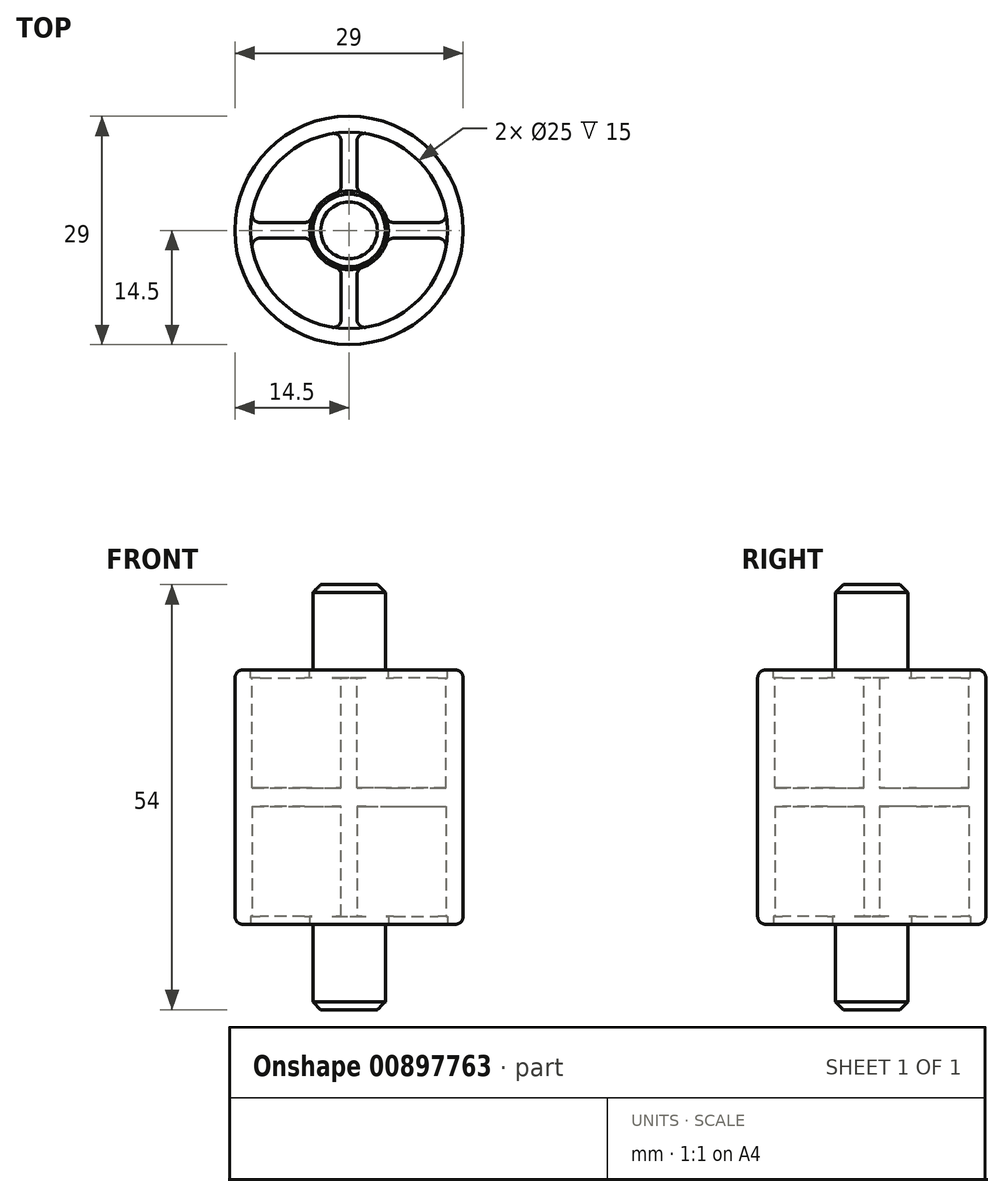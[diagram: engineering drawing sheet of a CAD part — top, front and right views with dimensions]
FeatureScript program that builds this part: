
annotation { "Feature Type Name" : "Feature", "Feature Type Description" : "" }
export const myFeature = defineFeature(function(context is Context, id is Id, definition is map)
    precondition{}
    {
        {
            var Q0;
            Q0=qCreatedBy(makeId("Front.planeOp"),FACE);
            var sketch = newSketch(context, id + "F0", { "sketchPlane" : qUnion([Q0])});
            skLineSegment(sketch, "E0", {"start": v(0, 27) * mm, "end": v(0, -27) * mm});
            skLineSegment(sketch, "E1", {"start": v(0, -27) * mm, "end": v(4.6, -27) * mm});
            skLineSegment(sketch, "E2", {"start": v(4.6, -27) * mm, "end": v(4.6, -16.15) * mm});
            skLineSegment(sketch, "E3", {"start": v(4.6, -16.15) * mm, "end": v(14.5, -16.15) * mm});
            skLineSegment(sketch, "E4", {"start": v(14.5, -16.15) * mm, "end": v(14.5, 16.15) * mm});
            skLineSegment(sketch, "E5", {"start": v(14.5, 16.15) * mm, "end": v(4.6, 16.15) * mm});
            skLineSegment(sketch, "E6", {"start": v(4.6, 16.15) * mm, "end": v(4.6, 27) * mm});
            skLineSegment(sketch, "E7", {"start": v(4.6, 27) * mm, "end": v(0, 27) * mm});
            skSolve(sketch);
        }
        {
            var Q0;
            Q0=makeQuery(id+"F0.imprint","IMPRINT",FACE,{"disambiguationData":[TD([[makeQuery(id+"F0.imprint","IMPRINT",EDGE,{"derivedFrom":sQuery(id+"F0.wireOp",EDGE,"E0")}),1.0]])]});
            var Q1;
            Q1=sQuery(id+"F0.wireOp",EDGE,"E0");
            revolve(context, id + "F1", {"surfaceOperationType" : NewSurfaceOperationType.NEW, "entities" : qUnion([Q0]), "axis" : qUnion([Q1]), "revolveType" : RevolveType.FULL});
        }
        {
            var Q0;
            Q0=makeQuery(id+"F1.opRevolve","SWEPT_FACE",FACE,{"disambiguationData":[OSD([sQuery(id+"F0.wireOp",EDGE,"E5")])]});
            var sketch = newSketch(context, id + "F2", { "sketchPlane" : qUnion([Q0])});
            skArc(sketch, "E8", {"start": v(12.46, 1) * mm, "mid": v(8.84, 8.84) * mm, "end": v(1, 12.46) * mm});
            skArc(sketch, "E9", {"start": v(4.9, 1) * mm, "mid": v(3.54, 3.54) * mm, "end": v(1, 4.9) * mm});
            skLineSegment(sketch, "E10", {"start": v(1, 4.9) * mm, "end": v(1, 12.46) * mm});
            skLineSegment(sketch, "E11", {"start": v(4.9, 1) * mm, "end": v(12.46, 1) * mm});
            skSolve(sketch);
        }
        {
            var Q0;
            Q0=makeQuery(id+"F2.imprint","IMPRINT",FACE,{"disambiguationData":[TD([[makeQuery(id+"F2.imprint","IMPRINT",EDGE,{"derivedFrom":sQuery(id+"F2.wireOp",EDGE,"E8")}),1.0]])]});
            extrude(context, id + "F3", {"entities" : qUnion([Q0]), "oppositeDirection" : true, "depth" : 15 * mm, "offsetDistance" : 25 * mm});
        }
        {
            var Q0;
            Q0=makeQuery(id+"F3.opExtrude","SWEPT_BODY",BODY,{"disambiguationData":[OSD([sQuery(id+"F2.wireOp",EDGE,"E8"),sQuery(id+"F2.wireOp",EDGE,"E9"),sQuery(id+"F2.wireOp",EDGE,"E10"),sQuery(id+"F2.wireOp",EDGE,"E11")])]});
            var Q1;
            Q1=makeQuery(id+"F1.opRevolve","SWEPT_FACE",FACE,{"disambiguationData":[OSD([sQuery(id+"F0.wireOp",EDGE,"E6")])]});
            circularPattern(context, id + "F4", {"entities" : qUnion([Q0]), "axis" : qUnion([Q1]), "angle" : 360 * degree, "instanceCount" : 4, "equalSpace" : true});
        }
        {
            var Q0;
            Q0=makeQuery(id+"F3.opExtrude","SWEPT_BODY",BODY,{"disambiguationData":[OSD([sQuery(id+"F2.wireOp",EDGE,"E8"),sQuery(id+"F2.wireOp",EDGE,"E9"),sQuery(id+"F2.wireOp",EDGE,"E10"),sQuery(id+"F2.wireOp",EDGE,"E11")])]});
            var Q1;
            Q1=makeQuery(id+"F4.opPattern","COPY",BODY,{"derivedFrom":makeQuery(id+"F3.opExtrude","SWEPT_BODY",BODY,{"disambiguationData":[OSD([sQuery(id+"F2.wireOp",EDGE,"E8"),sQuery(id+"F2.wireOp",EDGE,"E9"),sQuery(id+"F2.wireOp",EDGE,"E10"),sQuery(id+"F2.wireOp",EDGE,"E11")])]}),"instanceName":"1"});
            var Q2;
            Q2=makeQuery(id+"F4.opPattern","COPY",BODY,{"derivedFrom":makeQuery(id+"F3.opExtrude","SWEPT_BODY",BODY,{"disambiguationData":[OSD([sQuery(id+"F2.wireOp",EDGE,"E8"),sQuery(id+"F2.wireOp",EDGE,"E9"),sQuery(id+"F2.wireOp",EDGE,"E10"),sQuery(id+"F2.wireOp",EDGE,"E11")])]}),"instanceName":"2"});
            var Q3;
            Q3=makeQuery(id+"F4.opPattern","COPY",BODY,{"derivedFrom":makeQuery(id+"F3.opExtrude","SWEPT_BODY",BODY,{"disambiguationData":[OSD([sQuery(id+"F2.wireOp",EDGE,"E8"),sQuery(id+"F2.wireOp",EDGE,"E9"),sQuery(id+"F2.wireOp",EDGE,"E10"),sQuery(id+"F2.wireOp",EDGE,"E11")])]}),"instanceName":"3"});
            var Q4;
            Q4=qCreatedBy(makeId("Top.planeOp"),FACE);
            mirror(context, id + "F5", {"entities" : qUnion([Q0, Q1, Q2, Q3]), "mirrorPlane" : qUnion([Q4])});
        }
        {
            var Q0;
            Q0=makeQuery(id+"F3.opExtrude","SWEPT_BODY",BODY,{"disambiguationData":[OSD([sQuery(id+"F2.wireOp",EDGE,"E8"),sQuery(id+"F2.wireOp",EDGE,"E9"),sQuery(id+"F2.wireOp",EDGE,"E10"),sQuery(id+"F2.wireOp",EDGE,"E11")])]});
            var Q1;
            Q1=makeQuery(id+"F4.opPattern","COPY",BODY,{"derivedFrom":makeQuery(id+"F3.opExtrude","SWEPT_BODY",BODY,{"disambiguationData":[OSD([sQuery(id+"F2.wireOp",EDGE,"E8"),sQuery(id+"F2.wireOp",EDGE,"E9"),sQuery(id+"F2.wireOp",EDGE,"E10"),sQuery(id+"F2.wireOp",EDGE,"E11")])]}),"instanceName":"1"});
            var Q2;
            Q2=makeQuery(id+"F4.opPattern","COPY",BODY,{"derivedFrom":makeQuery(id+"F3.opExtrude","SWEPT_BODY",BODY,{"disambiguationData":[OSD([sQuery(id+"F2.wireOp",EDGE,"E8"),sQuery(id+"F2.wireOp",EDGE,"E9"),sQuery(id+"F2.wireOp",EDGE,"E10"),sQuery(id+"F2.wireOp",EDGE,"E11")])]}),"instanceName":"2"});
            var Q3;
            Q3=makeQuery(id+"F4.opPattern","COPY",BODY,{"derivedFrom":makeQuery(id+"F3.opExtrude","SWEPT_BODY",BODY,{"disambiguationData":[OSD([sQuery(id+"F2.wireOp",EDGE,"E8"),sQuery(id+"F2.wireOp",EDGE,"E9"),sQuery(id+"F2.wireOp",EDGE,"E10"),sQuery(id+"F2.wireOp",EDGE,"E11")])]}),"instanceName":"3"});
            var Q4;
            Q4=makeQuery(id+"F5.opPattern","COPY",BODY,{"derivedFrom":makeQuery(id+"F3.opExtrude","SWEPT_BODY",BODY,{"disambiguationData":[OSD([sQuery(id+"F2.wireOp",EDGE,"E8"),sQuery(id+"F2.wireOp",EDGE,"E9"),sQuery(id+"F2.wireOp",EDGE,"E10"),sQuery(id+"F2.wireOp",EDGE,"E11")])]}),"instanceName":"1"});
            var Q5;
            Q5=makeQuery(id+"F5.opPattern","COPY",BODY,{"derivedFrom":makeQuery(id+"F4.opPattern","COPY",BODY,{"derivedFrom":makeQuery(id+"F3.opExtrude","SWEPT_BODY",BODY,{"disambiguationData":[OSD([sQuery(id+"F2.wireOp",EDGE,"E8"),sQuery(id+"F2.wireOp",EDGE,"E9"),sQuery(id+"F2.wireOp",EDGE,"E10"),sQuery(id+"F2.wireOp",EDGE,"E11")])]}),"instanceName":"1"}),"instanceName":"1"});
            var Q6;
            Q6=makeQuery(id+"F5.opPattern","COPY",BODY,{"derivedFrom":makeQuery(id+"F4.opPattern","COPY",BODY,{"derivedFrom":makeQuery(id+"F3.opExtrude","SWEPT_BODY",BODY,{"disambiguationData":[OSD([sQuery(id+"F2.wireOp",EDGE,"E8"),sQuery(id+"F2.wireOp",EDGE,"E9"),sQuery(id+"F2.wireOp",EDGE,"E10"),sQuery(id+"F2.wireOp",EDGE,"E11")])]}),"instanceName":"2"}),"instanceName":"1"});
            var Q7;
            Q7=makeQuery(id+"F5.opPattern","COPY",BODY,{"derivedFrom":makeQuery(id+"F4.opPattern","COPY",BODY,{"derivedFrom":makeQuery(id+"F3.opExtrude","SWEPT_BODY",BODY,{"disambiguationData":[OSD([sQuery(id+"F2.wireOp",EDGE,"E8"),sQuery(id+"F2.wireOp",EDGE,"E9"),sQuery(id+"F2.wireOp",EDGE,"E10"),sQuery(id+"F2.wireOp",EDGE,"E11")])]}),"instanceName":"3"}),"instanceName":"1"});
            var Q8;
            Q8=makeQuery(id+"F1.opRevolve","SWEPT_BODY",BODY,{"disambiguationData":[OSD([sQuery(id+"F0.wireOp",EDGE,"E0"),sQuery(id+"F0.wireOp",EDGE,"E1"),sQuery(id+"F0.wireOp",EDGE,"E2"),sQuery(id+"F0.wireOp",EDGE,"E3"),sQuery(id+"F0.wireOp",EDGE,"E4"),sQuery(id+"F0.wireOp",EDGE,"E5"),sQuery(id+"F0.wireOp",EDGE,"E6"),sQuery(id+"F0.wireOp",EDGE,"E7")])]});
            booleanBodies(context, id + "F6", {"operationType" : BooleanOperationType.SUBTRACTION, "tools" : qUnion([Q0, Q1, Q2, Q3, Q4, Q5, Q6, Q7]), "targets" : qUnion([Q8])});
        }
        {
            var Q0;
            Q0=makeQuery(id+"F1.opRevolve","SWEPT_FACE",FACE,{"disambiguationData":[OSD([sQuery(id+"F0.wireOp",EDGE,"E5")])]});
            var sketch = newSketch(context, id + "F7", { "sketchPlane" : qUnion([Q0])});
            skCircle(sketch, "E12", {"center": v(0, 0) * mm, "radius": 12.5 * mm});
            skCircle(sketch, "E13", {"center": v(0, 0) * mm, "radius": 5 * mm});
            skSolve(sketch);
        }
        {
            var Q0;
            Q0 = qSketchRegion(id + "F7", true);
            extrude(context, id + "F8", {"entities" : qUnion([Q0]), "oppositeDirection" : true, "depth" : 1 * mm, "offsetDistance" : 25 * mm});
        }
        {
            var Q0;
            Q0=makeQuery(id+"F8.opExtrude","SWEPT_BODY",BODY,{"disambiguationData":[OSD([sQuery(id+"F7.wireOp",EDGE,"E12"),sQuery(id+"F7.wireOp",EDGE,"E13")])]});
            var Q1;
            Q1=qCreatedBy(makeId("Top.planeOp"),FACE);
            mirror(context, id + "F9", {"entities" : qUnion([Q0]), "mirrorPlane" : qUnion([Q1])});
        }
        {
            var Q0;
            Q0=makeQuery(id+"F8.opExtrude","SWEPT_BODY",BODY,{"disambiguationData":[OSD([sQuery(id+"F7.wireOp",EDGE,"E12"),sQuery(id+"F7.wireOp",EDGE,"E13")])]});
            var Q1;
            Q1=makeQuery(id+"F9.opPattern","COPY",BODY,{"derivedFrom":makeQuery(id+"F8.opExtrude","SWEPT_BODY",BODY,{"disambiguationData":[OSD([sQuery(id+"F7.wireOp",EDGE,"E12"),sQuery(id+"F7.wireOp",EDGE,"E13")])]}),"instanceName":"1"});
            var Q2;
            Q2=makeQuery(id+"F1.opRevolve","SWEPT_BODY",BODY,{"disambiguationData":[OSD([sQuery(id+"F0.wireOp",EDGE,"E0"),sQuery(id+"F0.wireOp",EDGE,"E1"),sQuery(id+"F0.wireOp",EDGE,"E2"),sQuery(id+"F0.wireOp",EDGE,"E3"),sQuery(id+"F0.wireOp",EDGE,"E4"),sQuery(id+"F0.wireOp",EDGE,"E5"),sQuery(id+"F0.wireOp",EDGE,"E6"),sQuery(id+"F0.wireOp",EDGE,"E7")])]});
            booleanBodies(context, id + "F10", {"operationType" : BooleanOperationType.SUBTRACTION, "tools" : qUnion([Q0, Q1]), "targets" : qUnion([Q2])});
        }
        {
            var Q0;
            Q0=makeQuery(id+"F1.opRevolve","SWEPT_EDGE",EDGE,{"disambiguationData":[OSD([sQuery(id+"F0.wireOp",EDGE,"E4"),sQuery(id+"F0.wireOp",EDGE,"E5")])]});
            var Q1;
            Q1=makeQuery(id+"F1.opRevolve","SWEPT_EDGE",EDGE,{"disambiguationData":[OSD([sQuery(id+"F0.wireOp",EDGE,"E3"),sQuery(id+"F0.wireOp",EDGE,"E4")])]});
            fillet(context, id + "F11", {"entities" : qUnion([Q0, Q1]), "radius" : 1 * mm, "tangentPropagation" : true, "allowEdgeOverflow" : false});
        }
        {
            var Q0;
            Q0=makeQuery(id+"F6.opBoolean","COPY",EDGE,{"derivedFrom":makeQuery(id+"F5.opPattern","COPY",EDGE,{"derivedFrom":makeQuery(id+"F4.opPattern","COPY",EDGE,{"derivedFrom":makeQuery(id+"F3.opExtrude","SWEPT_EDGE",EDGE,{"disambiguationData":[OSD([sQuery(id+"F2.wireOp",EDGE,"E8"),sQuery(id+"F2.wireOp",EDGE,"E10")])]}),"instanceName":"2"}),"instanceName":"1"})});
            var Q1;
            Q1=makeQuery(id+"F6.opBoolean","COPY",EDGE,{"derivedFrom":makeQuery(id+"F5.opPattern","COPY",EDGE,{"derivedFrom":makeQuery(id+"F4.opPattern","COPY",EDGE,{"derivedFrom":makeQuery(id+"F3.opExtrude","SWEPT_EDGE",EDGE,{"disambiguationData":[OSD([sQuery(id+"F2.wireOp",EDGE,"E8"),sQuery(id+"F2.wireOp",EDGE,"E11")])]}),"instanceName":"3"}),"instanceName":"1"})});
            var Q2;
            Q2=makeQuery(id+"F6.opBoolean","COPY",EDGE,{"derivedFrom":makeQuery(id+"F5.opPattern","COPY",EDGE,{"derivedFrom":makeQuery(id+"F4.opPattern","COPY",EDGE,{"derivedFrom":makeQuery(id+"F3.opExtrude","SWEPT_EDGE",EDGE,{"disambiguationData":[OSD([sQuery(id+"F2.wireOp",EDGE,"E9"),sQuery(id+"F2.wireOp",EDGE,"E11")])]}),"instanceName":"3"}),"instanceName":"1"})});
            var Q3;
            Q3=makeQuery(id+"F6.opBoolean","COPY",EDGE,{"derivedFrom":makeQuery(id+"F5.opPattern","COPY",EDGE,{"derivedFrom":makeQuery(id+"F4.opPattern","COPY",EDGE,{"derivedFrom":makeQuery(id+"F3.opExtrude","SWEPT_EDGE",EDGE,{"disambiguationData":[OSD([sQuery(id+"F2.wireOp",EDGE,"E9"),sQuery(id+"F2.wireOp",EDGE,"E10")])]}),"instanceName":"3"}),"instanceName":"1"})});
            var Q4;
            Q4=makeQuery(id+"F6.opBoolean","COPY",EDGE,{"derivedFrom":makeQuery(id+"F5.opPattern","COPY",EDGE,{"derivedFrom":makeQuery(id+"F4.opPattern","COPY",EDGE,{"derivedFrom":makeQuery(id+"F3.opExtrude","SWEPT_EDGE",EDGE,{"disambiguationData":[OSD([sQuery(id+"F2.wireOp",EDGE,"E8"),sQuery(id+"F2.wireOp",EDGE,"E10")])]}),"instanceName":"3"}),"instanceName":"1"})});
            var Q5;
            Q5=makeQuery(id+"F6.opBoolean","COPY",EDGE,{"derivedFrom":makeQuery(id+"F5.opPattern","COPY",EDGE,{"derivedFrom":makeQuery(id+"F3.opExtrude","SWEPT_EDGE",EDGE,{"disambiguationData":[OSD([sQuery(id+"F2.wireOp",EDGE,"E9"),sQuery(id+"F2.wireOp",EDGE,"E11")])]}),"instanceName":"1"})});
            var Q6;
            Q6=makeQuery(id+"F6.opBoolean","COPY",EDGE,{"derivedFrom":makeQuery(id+"F5.opPattern","COPY",EDGE,{"derivedFrom":makeQuery(id+"F3.opExtrude","SWEPT_EDGE",EDGE,{"disambiguationData":[OSD([sQuery(id+"F2.wireOp",EDGE,"E8"),sQuery(id+"F2.wireOp",EDGE,"E11")])]}),"instanceName":"1"})});
            var Q7;
            Q7=makeQuery(id+"F6.opBoolean","COPY",EDGE,{"derivedFrom":makeQuery(id+"F5.opPattern","COPY",EDGE,{"derivedFrom":makeQuery(id+"F3.opExtrude","SWEPT_EDGE",EDGE,{"disambiguationData":[OSD([sQuery(id+"F2.wireOp",EDGE,"E9"),sQuery(id+"F2.wireOp",EDGE,"E10")])]}),"instanceName":"1"})});
            var Q8;
            Q8=makeQuery(id+"F6.opBoolean","COPY",EDGE,{"derivedFrom":makeQuery(id+"F5.opPattern","COPY",EDGE,{"derivedFrom":makeQuery(id+"F3.opExtrude","SWEPT_EDGE",EDGE,{"disambiguationData":[OSD([sQuery(id+"F2.wireOp",EDGE,"E8"),sQuery(id+"F2.wireOp",EDGE,"E10")])]}),"instanceName":"1"})});
            var Q9;
            Q9=makeQuery(id+"F6.opBoolean","COPY",EDGE,{"derivedFrom":makeQuery(id+"F5.opPattern","COPY",EDGE,{"derivedFrom":makeQuery(id+"F4.opPattern","COPY",EDGE,{"derivedFrom":makeQuery(id+"F3.opExtrude","SWEPT_EDGE",EDGE,{"disambiguationData":[OSD([sQuery(id+"F2.wireOp",EDGE,"E9"),sQuery(id+"F2.wireOp",EDGE,"E11")])]}),"instanceName":"1"}),"instanceName":"1"})});
            var Q10;
            Q10=makeQuery(id+"F6.opBoolean","COPY",EDGE,{"derivedFrom":makeQuery(id+"F5.opPattern","COPY",EDGE,{"derivedFrom":makeQuery(id+"F4.opPattern","COPY",EDGE,{"derivedFrom":makeQuery(id+"F3.opExtrude","SWEPT_EDGE",EDGE,{"disambiguationData":[OSD([sQuery(id+"F2.wireOp",EDGE,"E8"),sQuery(id+"F2.wireOp",EDGE,"E11")])]}),"instanceName":"1"}),"instanceName":"1"})});
            var Q11;
            Q11=makeQuery(id+"F6.opBoolean","COPY",EDGE,{"derivedFrom":makeQuery(id+"F5.opPattern","COPY",EDGE,{"derivedFrom":makeQuery(id+"F4.opPattern","COPY",EDGE,{"derivedFrom":makeQuery(id+"F3.opExtrude","SWEPT_EDGE",EDGE,{"disambiguationData":[OSD([sQuery(id+"F2.wireOp",EDGE,"E9"),sQuery(id+"F2.wireOp",EDGE,"E10")])]}),"instanceName":"1"}),"instanceName":"1"})});
            var Q12;
            Q12=makeQuery(id+"F6.opBoolean","COPY",EDGE,{"derivedFrom":makeQuery(id+"F5.opPattern","COPY",EDGE,{"derivedFrom":makeQuery(id+"F4.opPattern","COPY",EDGE,{"derivedFrom":makeQuery(id+"F3.opExtrude","SWEPT_EDGE",EDGE,{"disambiguationData":[OSD([sQuery(id+"F2.wireOp",EDGE,"E8"),sQuery(id+"F2.wireOp",EDGE,"E10")])]}),"instanceName":"1"}),"instanceName":"1"})});
            var Q13;
            Q13=makeQuery(id+"F6.opBoolean","COPY",EDGE,{"derivedFrom":makeQuery(id+"F5.opPattern","COPY",EDGE,{"derivedFrom":makeQuery(id+"F4.opPattern","COPY",EDGE,{"derivedFrom":makeQuery(id+"F3.opExtrude","SWEPT_EDGE",EDGE,{"disambiguationData":[OSD([sQuery(id+"F2.wireOp",EDGE,"E9"),sQuery(id+"F2.wireOp",EDGE,"E10")])]}),"instanceName":"2"}),"instanceName":"1"})});
            var Q14;
            Q14=makeQuery(id+"F6.opBoolean","COPY",EDGE,{"derivedFrom":makeQuery(id+"F5.opPattern","COPY",EDGE,{"derivedFrom":makeQuery(id+"F4.opPattern","COPY",EDGE,{"derivedFrom":makeQuery(id+"F3.opExtrude","SWEPT_EDGE",EDGE,{"disambiguationData":[OSD([sQuery(id+"F2.wireOp",EDGE,"E9"),sQuery(id+"F2.wireOp",EDGE,"E11")])]}),"instanceName":"2"}),"instanceName":"1"})});
            var Q15;
            Q15=makeQuery(id+"F6.opBoolean","COPY",EDGE,{"derivedFrom":makeQuery(id+"F5.opPattern","COPY",EDGE,{"derivedFrom":makeQuery(id+"F4.opPattern","COPY",EDGE,{"derivedFrom":makeQuery(id+"F3.opExtrude","SWEPT_EDGE",EDGE,{"disambiguationData":[OSD([sQuery(id+"F2.wireOp",EDGE,"E8"),sQuery(id+"F2.wireOp",EDGE,"E11")])]}),"instanceName":"2"}),"instanceName":"1"})});
            var Q16;
            Q16=makeQuery(id+"F6.opBoolean","COPY",EDGE,{"derivedFrom":makeQuery(id+"F4.opPattern","COPY",EDGE,{"derivedFrom":makeQuery(id+"F3.opExtrude","SWEPT_EDGE",EDGE,{"disambiguationData":[OSD([sQuery(id+"F2.wireOp",EDGE,"E9"),sQuery(id+"F2.wireOp",EDGE,"E10")])]}),"instanceName":"2"})});
            var Q17;
            Q17=makeQuery(id+"F6.opBoolean","COPY",EDGE,{"derivedFrom":makeQuery(id+"F4.opPattern","COPY",EDGE,{"derivedFrom":makeQuery(id+"F3.opExtrude","SWEPT_EDGE",EDGE,{"disambiguationData":[OSD([sQuery(id+"F2.wireOp",EDGE,"E8"),sQuery(id+"F2.wireOp",EDGE,"E10")])]}),"instanceName":"2"})});
            var Q18;
            Q18=makeQuery(id+"F6.opBoolean","COPY",EDGE,{"derivedFrom":makeQuery(id+"F4.opPattern","COPY",EDGE,{"derivedFrom":makeQuery(id+"F3.opExtrude","SWEPT_EDGE",EDGE,{"disambiguationData":[OSD([sQuery(id+"F2.wireOp",EDGE,"E9"),sQuery(id+"F2.wireOp",EDGE,"E11")])]}),"instanceName":"3"})});
            var Q19;
            Q19=makeQuery(id+"F6.opBoolean","COPY",EDGE,{"derivedFrom":makeQuery(id+"F4.opPattern","COPY",EDGE,{"derivedFrom":makeQuery(id+"F3.opExtrude","SWEPT_EDGE",EDGE,{"disambiguationData":[OSD([sQuery(id+"F2.wireOp",EDGE,"E8"),sQuery(id+"F2.wireOp",EDGE,"E11")])]}),"instanceName":"3"})});
            var Q20;
            Q20=makeQuery(id+"F6.opBoolean","COPY",EDGE,{"derivedFrom":makeQuery(id+"F4.opPattern","COPY",EDGE,{"derivedFrom":makeQuery(id+"F3.opExtrude","SWEPT_EDGE",EDGE,{"disambiguationData":[OSD([sQuery(id+"F2.wireOp",EDGE,"E9"),sQuery(id+"F2.wireOp",EDGE,"E11")])]}),"instanceName":"2"})});
            var Q21;
            Q21=makeQuery(id+"F6.opBoolean","COPY",EDGE,{"derivedFrom":makeQuery(id+"F4.opPattern","COPY",EDGE,{"derivedFrom":makeQuery(id+"F3.opExtrude","SWEPT_EDGE",EDGE,{"disambiguationData":[OSD([sQuery(id+"F2.wireOp",EDGE,"E8"),sQuery(id+"F2.wireOp",EDGE,"E11")])]}),"instanceName":"2"})});
            var Q22;
            Q22=makeQuery(id+"F6.opBoolean","COPY",EDGE,{"derivedFrom":makeQuery(id+"F4.opPattern","COPY",EDGE,{"derivedFrom":makeQuery(id+"F3.opExtrude","SWEPT_EDGE",EDGE,{"disambiguationData":[OSD([sQuery(id+"F2.wireOp",EDGE,"E8"),sQuery(id+"F2.wireOp",EDGE,"E10")])]}),"instanceName":"1"})});
            var Q23;
            Q23=makeQuery(id+"F6.opBoolean","COPY",EDGE,{"derivedFrom":makeQuery(id+"F4.opPattern","COPY",EDGE,{"derivedFrom":makeQuery(id+"F3.opExtrude","SWEPT_EDGE",EDGE,{"disambiguationData":[OSD([sQuery(id+"F2.wireOp",EDGE,"E9"),sQuery(id+"F2.wireOp",EDGE,"E10")])]}),"instanceName":"1"})});
            var Q24;
            Q24=makeQuery(id+"F6.opBoolean","COPY",EDGE,{"derivedFrom":makeQuery(id+"F4.opPattern","COPY",EDGE,{"derivedFrom":makeQuery(id+"F3.opExtrude","SWEPT_EDGE",EDGE,{"disambiguationData":[OSD([sQuery(id+"F2.wireOp",EDGE,"E8"),sQuery(id+"F2.wireOp",EDGE,"E11")])]}),"instanceName":"1"})});
            var Q25;
            Q25=makeQuery(id+"F6.opBoolean","COPY",EDGE,{"derivedFrom":makeQuery(id+"F4.opPattern","COPY",EDGE,{"derivedFrom":makeQuery(id+"F3.opExtrude","SWEPT_EDGE",EDGE,{"disambiguationData":[OSD([sQuery(id+"F2.wireOp",EDGE,"E9"),sQuery(id+"F2.wireOp",EDGE,"E11")])]}),"instanceName":"1"})});
            var Q26;
            Q26=makeQuery(id+"F6.opBoolean","COPY",EDGE,{"derivedFrom":makeQuery(id+"F3.opExtrude","SWEPT_EDGE",EDGE,{"disambiguationData":[OSD([sQuery(id+"F2.wireOp",EDGE,"E9"),sQuery(id+"F2.wireOp",EDGE,"E10")])]})});
            var Q27;
            Q27=makeQuery(id+"F6.opBoolean","COPY",EDGE,{"derivedFrom":makeQuery(id+"F3.opExtrude","SWEPT_EDGE",EDGE,{"disambiguationData":[OSD([sQuery(id+"F2.wireOp",EDGE,"E8"),sQuery(id+"F2.wireOp",EDGE,"E10")])]})});
            var Q28;
            Q28=makeQuery(id+"F6.opBoolean","COPY",EDGE,{"derivedFrom":makeQuery(id+"F3.opExtrude","SWEPT_EDGE",EDGE,{"disambiguationData":[OSD([sQuery(id+"F2.wireOp",EDGE,"E9"),sQuery(id+"F2.wireOp",EDGE,"E11")])]})});
            var Q29;
            Q29=makeQuery(id+"F6.opBoolean","COPY",EDGE,{"derivedFrom":makeQuery(id+"F3.opExtrude","SWEPT_EDGE",EDGE,{"disambiguationData":[OSD([sQuery(id+"F2.wireOp",EDGE,"E8"),sQuery(id+"F2.wireOp",EDGE,"E11")])]})});
            var Q30;
            Q30=makeQuery(id+"F6.opBoolean","COPY",EDGE,{"derivedFrom":makeQuery(id+"F4.opPattern","COPY",EDGE,{"derivedFrom":makeQuery(id+"F3.opExtrude","SWEPT_EDGE",EDGE,{"disambiguationData":[OSD([sQuery(id+"F2.wireOp",EDGE,"E9"),sQuery(id+"F2.wireOp",EDGE,"E10")])]}),"instanceName":"3"})});
            var Q31;
            Q31=makeQuery(id+"F6.opBoolean","COPY",EDGE,{"derivedFrom":makeQuery(id+"F4.opPattern","COPY",EDGE,{"derivedFrom":makeQuery(id+"F3.opExtrude","SWEPT_EDGE",EDGE,{"disambiguationData":[OSD([sQuery(id+"F2.wireOp",EDGE,"E8"),sQuery(id+"F2.wireOp",EDGE,"E10")])]}),"instanceName":"3"})});
            fillet(context, id + "F12", {"entities" : qUnion([Q0, Q1, Q2, Q3, Q4, Q5, Q6, Q7, Q8, Q9, Q10, Q11, Q12, Q13, Q14, Q15, Q16, Q17, Q18, Q19, Q20, Q21, Q22, Q23, Q24, Q25, Q26, Q27, Q28, Q29, Q30, Q31]), "radius" : 1 * mm, "tangentPropagation" : true, "allowEdgeOverflow" : false});
        }
        {
            var Q0;
            Q0=makeQuery(id+"F1.opRevolve","SWEPT_EDGE",EDGE,{"disambiguationData":[OSD([sQuery(id+"F0.wireOp",EDGE,"E6"),sQuery(id+"F0.wireOp",EDGE,"E7")])]});
            var Q1;
            Q1=makeQuery(id+"F1.opRevolve","SWEPT_EDGE",EDGE,{"disambiguationData":[OSD([sQuery(id+"F0.wireOp",EDGE,"E1"),sQuery(id+"F0.wireOp",EDGE,"E2")])]});
            chamfer(context, id + "F13", {"entities" : qUnion([Q0, Q1]), "width" : 1 * mm, "tangentPropagation" : true});
        }
    });
